# Revit family: Washer_Milnor_42044-SP2
name_source: partatom
category: Mechanical Equipment
units: mm (PartAtom-declared; Revit-internal decimal feet)

## family parameters
Always vertical = No
Classification Number = 23.45.70.11.14.11
Cut with Voids When Loaded = No
Maintain Annotation Orientation = No
Part Type = Normal
Room Calculation Point = No
Round Connector Dimension = Use Diameter
Shared = No
Work Plane-Based = Yes

## types (1)
- Washer_Milnor_42044-SP2
    Assembly Code = E1010610
    Cylinder Depth = 3' - 8"
    Cylinder Diameter = 3' - 6"
    Cylinder Volume = 0 CF
    Default Elevation = 4' - 0"
    Door Base from FF = 3' - 1"
    Door Opening Depth_Clean = 0' - 0"
    Door Opening Depth_Dirty = 2' - 4"
    Dynamic Load = 0.00 kip
    Expected Lifespan (Years) = 0
    Frequency = 0 Hz
    Keynote = 11110
    MEP Amperage = 0 A
    Maintenance Schedule (Months) = 0
    Manufacturer = Pellerin Milnor Corp
    Manufacturer Fax = 504-468-3094
    Manufacturer Website = http://www.milnor.com
    Model = As Specified
    Number of Poles = 1
    Phase = 0
    Product Data = http://www.arcat.com
    Revision = R1_04-2011
    Sales Information = http://www.milnor.com
    Send Message = http://www.arcat.com
    URL = http://www.milnor.com
    Unit Depth = 6' - 2 1/4"
    Unit Height = 6' - 9 5/8"
    Unit Weight = 0
    Unit Width = 7' - 5 1/4"
    Vibration Frequency = 0
    Voltage_MEP = 0 V
    Warranty Duration (Years) = 0
    doorgas = 2' - 4 1/2"

## geometry (parser evidence)
native form markers: Sweep x2
no freeform markers — native parametric forms only
